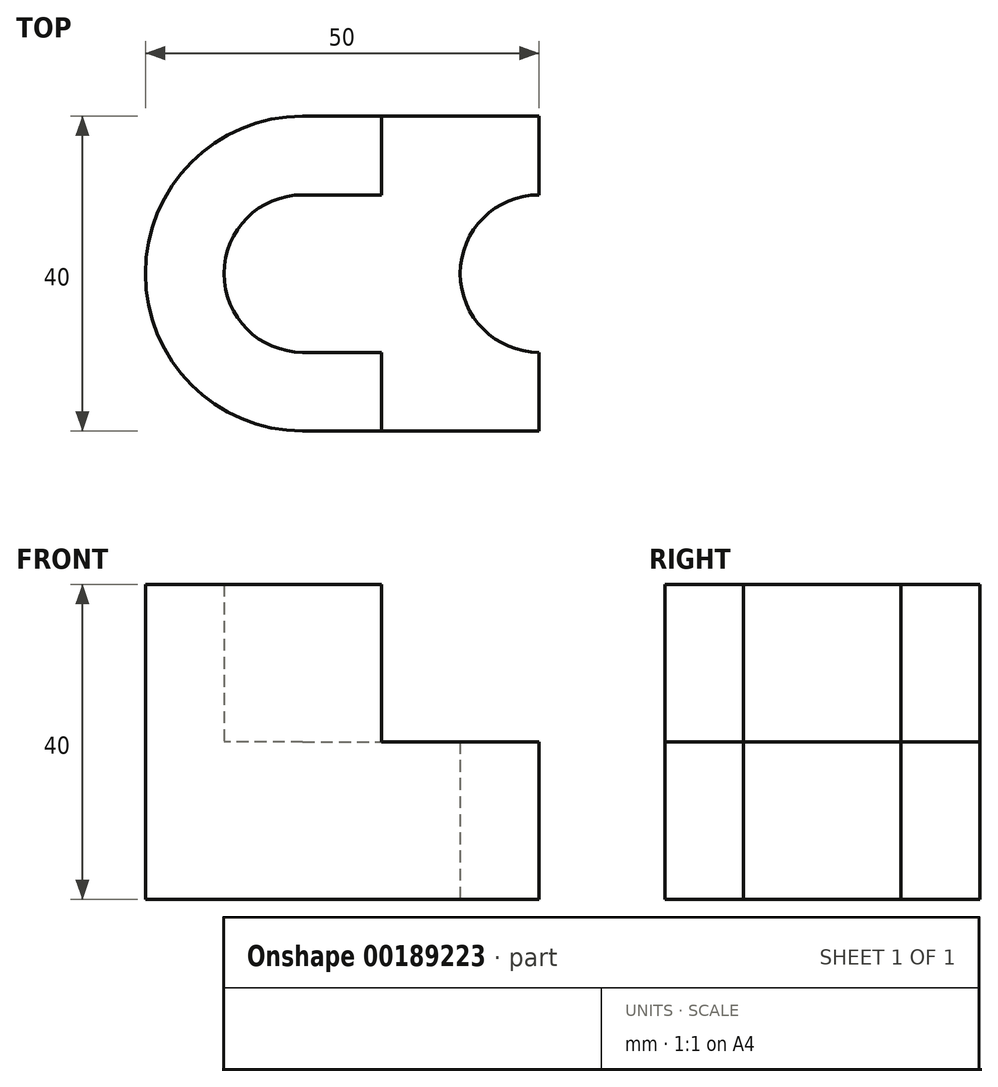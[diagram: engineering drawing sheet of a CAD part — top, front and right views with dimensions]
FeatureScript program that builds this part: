
annotation { "Feature Type Name" : "Feature", "Feature Type Description" : "" }
export const myFeature = defineFeature(function(context is Context, id is Id, definition is map)
    precondition{}
    {
        {
            var Q0;
            Q0=qCreatedBy(makeId("Top.planeOp"),FACE);
            var sketch = newSketch(context, id + "F0", { "sketchPlane" : qUnion([Q0])});
            skLineSegment(sketch, "E0.bottom", {"start": v(0, 0) * mm, "end": v(30, 0) * mm});
            skLineSegment(sketch, "E0.top", {"start": v(0, 40) * mm, "end": v(30, 40) * mm});
            skLineSegment(sketch, "E0.right", {"start": v(30, 0) * mm, "end": v(30, 10) * mm});
            skArc(sketch, "E1", {"start": v(0, 40) * mm, "mid": v(-20, 20) * mm, "end": v(0, 0) * mm});
            skArc(sketch, "E2", {"start": v(30, 30) * mm, "mid": v(20, 20) * mm, "end": v(30, 10) * mm});
            skLineSegment(sketch, "E3.trimOffspring", {"start": v(30, 30) * mm, "end": v(30, 40) * mm});
            skSolve(sketch);
        }
        {
            var Q0;
            Q0=makeQuery(id+"F0.imprint","IMPRINT",FACE,{"disambiguationData":[TD([[makeQuery(id+"F0.imprint","IMPRINT",EDGE,{"derivedFrom":sQuery(id+"F0.wireOp",EDGE,"E0.bottom")}),1.0]])]});
            extrude(context, id + "F1", {"entities" : qUnion([Q0]), "depth" : 20 * mm});
        }
        {
            var Q0;
            Q0=makeQuery(id+"F1.opExtrude","CAP_FACE",FACE,{"disambiguationData":[OSD([sQuery(id+"F0.wireOp",EDGE,"E0.bottom"),sQuery(id+"F0.wireOp",EDGE,"E0.top"),sQuery(id+"F0.wireOp",EDGE,"E0.right"),sQuery(id+"F0.wireOp",EDGE,"E1"),sQuery(id+"F0.wireOp",EDGE,"E2"),sQuery(id+"F0.wireOp",EDGE,"E3.trimOffspring")])],"isStart":false});
            var sketch = newSketch(context, id + "F2", { "sketchPlane" : qUnion([Q0])});
            skArc(sketch, "E4.0", {"start": v(0, 40) * mm, "mid": v(-20, 20) * mm, "end": v(0, 0) * mm});
            skLineSegment(sketch, "E5.0", {"start": v(0, 40) * mm, "end": v(10, 40) * mm});
            skLineSegment(sketch, "E6.0", {"start": v(0, 0) * mm, "end": v(10, 0) * mm});
            skLineSegment(sketch, "E7.0", {"start": v(0, 10) * mm, "end": v(10, 10) * mm});
            skArc(sketch, "E7.1", {"start": v(0, 30) * mm, "mid": v(-10, 20) * mm, "end": v(0, 10) * mm});
            skLineSegment(sketch, "E7.2", {"start": v(0, 30) * mm, "end": v(10, 30) * mm});
            skLineSegment(sketch, "E8", {"start": v(10, 40) * mm, "end": v(10, 30) * mm});
            skLineSegment(sketch, "E9", {"start": v(10, 10) * mm, "end": v(10, 0) * mm});
            skPoint(sketch, "E10.orphan", {"position": v(30, 40) * mm});
            skPoint(sketch, "E11.orphan", {"position": v(30, 0) * mm});
            skSolve(sketch);
        }
        {
            var Q0;
            Q0=makeQuery(id+"F2.imprint","IMPRINT",FACE,{"disambiguationData":[TD([[makeQuery(id+"F2.imprint","IMPRINT",EDGE,{"derivedFrom":sQuery(id+"F2.wireOp",EDGE,"E4.0")}),1.0]])]});
            extrude(context, id + "F3", {"entities" : qUnion([Q0]), "operationType" : NewBodyOperationType.ADD, "depth" : 20 * mm});
        }
    });
